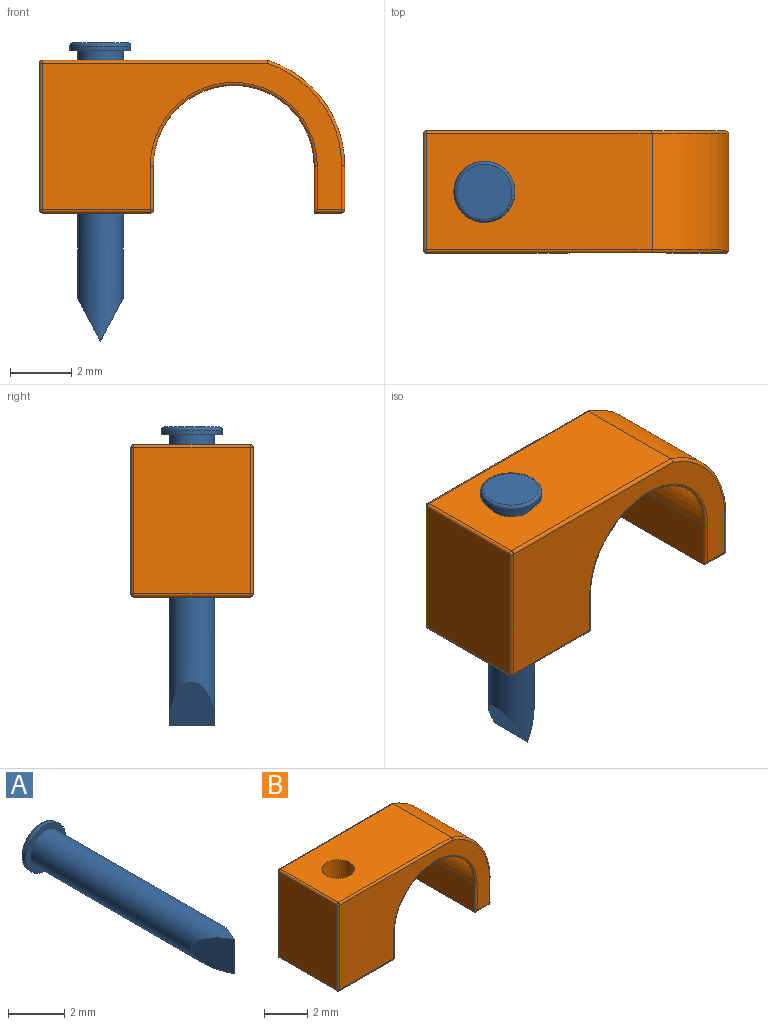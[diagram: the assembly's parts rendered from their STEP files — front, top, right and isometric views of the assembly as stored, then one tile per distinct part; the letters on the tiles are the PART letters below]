
ASSEMBLY  parts=2 mates=1
PART A: 7 faces, bbox 2.2x9.8x2.2 mm
  f0: cylinder r=0.75mm len=9.51mm, axis (0,1,0), area 40.6mm2, adj f2,f5,f6
  f1: cylinder r=1mm len=2mm, axis (0,1,0), area 0.9mm2, adj f2,f4
  f2: plane 2x2mm, normal (0,-1,0), area 1.4mm2, adj f0,f1
  f3: plane 1.8x1.8mm, normal (0,1,0), area 2.5mm2, adj f4
  f4: torus R=0.9mm, axis (0,-1,0), area 1mm2, adj f1,f3
  f5: plane 1.5x1.41mm, normal (0.88,-0.47,0), area 1.9mm2, adj f0,f6
  f6: plane 1.5x1.41mm, normal (-0.88,-0.47,0), area 1.9mm2, adj f0,f5
PART B: 42 faces, bbox 10.3x4x5.3 mm
  f0: plane 3.8x0.9mm, normal (0,0,-1), area 3.4mm2, adj f8,f24,f33,f38
  f1: plane 3.8x1.45mm, normal (1,0,0), area 5.5mm2, adj f2,f25,f33,f34
  f2: cylinder r=3.63mm len=3.8mm, axis (0,1,0), area 17.3mm2, adj f1,f3,f18,f30
  f3: plane 7.39x3.8mm, normal (0,0,1), area 26.3mm2, adj f2,f13,f14,f26,f41
  f4: plane 4.8x3.8mm, normal (-1,0,0), area 18.2mm2, adj f12,f14,f20,f21
  f5: plane 3.8x3.54mm, normal (0,0,-1), area 11.7mm2, adj f21,f22,f31,f32,f41
  f6: plane 3.8x1.44mm, normal (1,0,0), area 5.5mm2, adj f7,f23,f32,f37
  f7: cylinder r=2.63mm len=5.26mm, axis (0,1,0), area 31.4mm2, adj f6,f8,f16,f39
  f8: plane 3.8x1.55mm, normal (-1,0,0), area 5.9mm2, adj f0,f7,f17,f40
  f9: plane 9.8x4.8mm, normal (0,-1,0), area 25.2mm2, adj f12,f13,f16,f17,f18,f22,f23,f24
  f10: plane 9.8x4.8mm, normal (0,1,0), area 25.2mm2, adj f20,f26,f30,f31,f34,f37,f38,f39
  f11: sphere r=0.1mm, area 0mm2, adj f12,f13,f14
  f12: cylinder r=0.1mm len=4.8mm, axis (0,0,1), area 0.8mm2, adj f4,f9,f11,f15
  f13: cylinder r=0.1mm len=7.39mm, axis (1,0,0), area 1.2mm2, adj f3,f9,f11,f18
  f14: cylinder r=0.1mm len=3.8mm, axis (0,1,0), area 0.6mm2, adj f3,f4,f11,f19
  f15: sphere r=0.1mm, area 0mm2, adj f12,f21,f22
  f16: torus R=2.73mm, axis (0,-1,0), area 1.3mm2, adj f7,f9,f17,f23
  f17: cylinder r=0.1mm len=1.55mm, axis (0,0,1), area 0.2mm2, adj f8,f9,f16,f24
  f18: torus R=3.53mm, axis (0,-1,0), area 0.7mm2, adj f2,f9,f13,f25
  f19: sphere r=0.1mm, area 0mm2, adj f14,f20,f26
  f20: cylinder r=0.1mm len=4.8mm, axis (0,0,-1), area 0.8mm2, adj f4,f10,f19,f27
  f21: cylinder r=0.1mm len=3.8mm, axis (0,-1,0), area 0.6mm2, adj f4,f5,f15,f27
  f22: cylinder r=0.1mm len=3.54mm, axis (-1,0,0), area 0.6mm2, adj f5,f9,f15,f28
  f23: cylinder r=0.1mm len=1.44mm, axis (0,0,-1), area 0.2mm2, adj f6,f9,f16,f28
  f24: cylinder r=0.1mm len=0.9mm, axis (-1,0,0), area 0.1mm2, adj f0,f9,f17,f29
  f25: cylinder r=0.1mm len=1.45mm, axis (0,0,-1), area 0.2mm2, adj f1,f9,f18,f29
  f26: cylinder r=0.1mm len=7.39mm, axis (-1,0,0), area 1.2mm2, adj f3,f10,f19,f30
  f27: sphere r=0.1mm, area 0mm2, adj f20,f21,f31
  f28: sphere r=0.1mm, area 0mm2, adj f22,f23,f32
  f29: sphere r=0.1mm, area 0mm2, adj f24,f25,f33
  f30: torus R=3.53mm, axis (0,-1,0), area 0.7mm2, adj f2,f10,f26,f34
  f31: cylinder r=0.1mm len=3.54mm, axis (1,0,0), area 0.6mm2, adj f5,f10,f27,f35
  f32: cylinder r=0.1mm len=3.8mm, axis (0,1,0), area 0.6mm2, adj f5,f6,f28,f35
  f33: cylinder r=0.1mm len=3.8mm, axis (0,1,0), area 0.6mm2, adj f0,f1,f29,f36
  f34: cylinder r=0.1mm len=1.45mm, axis (0,0,1), area 0.2mm2, adj f1,f10,f30,f36
  f35: sphere r=0.1mm, area 0mm2, adj f31,f32,f37
  f36: sphere r=0.1mm, area 0mm2, adj f33,f34,f38
  f37: cylinder r=0.1mm len=1.44mm, axis (0,0,1), area 0.2mm2, adj f6,f10,f35,f39
  f38: cylinder r=0.1mm len=0.9mm, axis (1,0,0), area 0.1mm2, adj f0,f10,f36,f40
  f39: torus R=2.73mm, axis (0,-1,0), area 1.3mm2, adj f7,f10,f37,f40
  f40: cylinder r=0.1mm len=1.55mm, axis (0,0,-1), area 0.2mm2, adj f8,f10,f38,f39
  f41: cylinder r=0.75mm len=5mm, axis (0,0,1), area 23.6mm2, adj f3,f5
PLACE A rot(axis=(1,0,0),90deg) t=(2.65,-2.35,5.57)mm
PLACE B t=(0.65,-0.35,0)mm
MATE slider A.f0 <-> B.f41  axis (0,0,1) through (2.65,-2.35,0.53)mm
